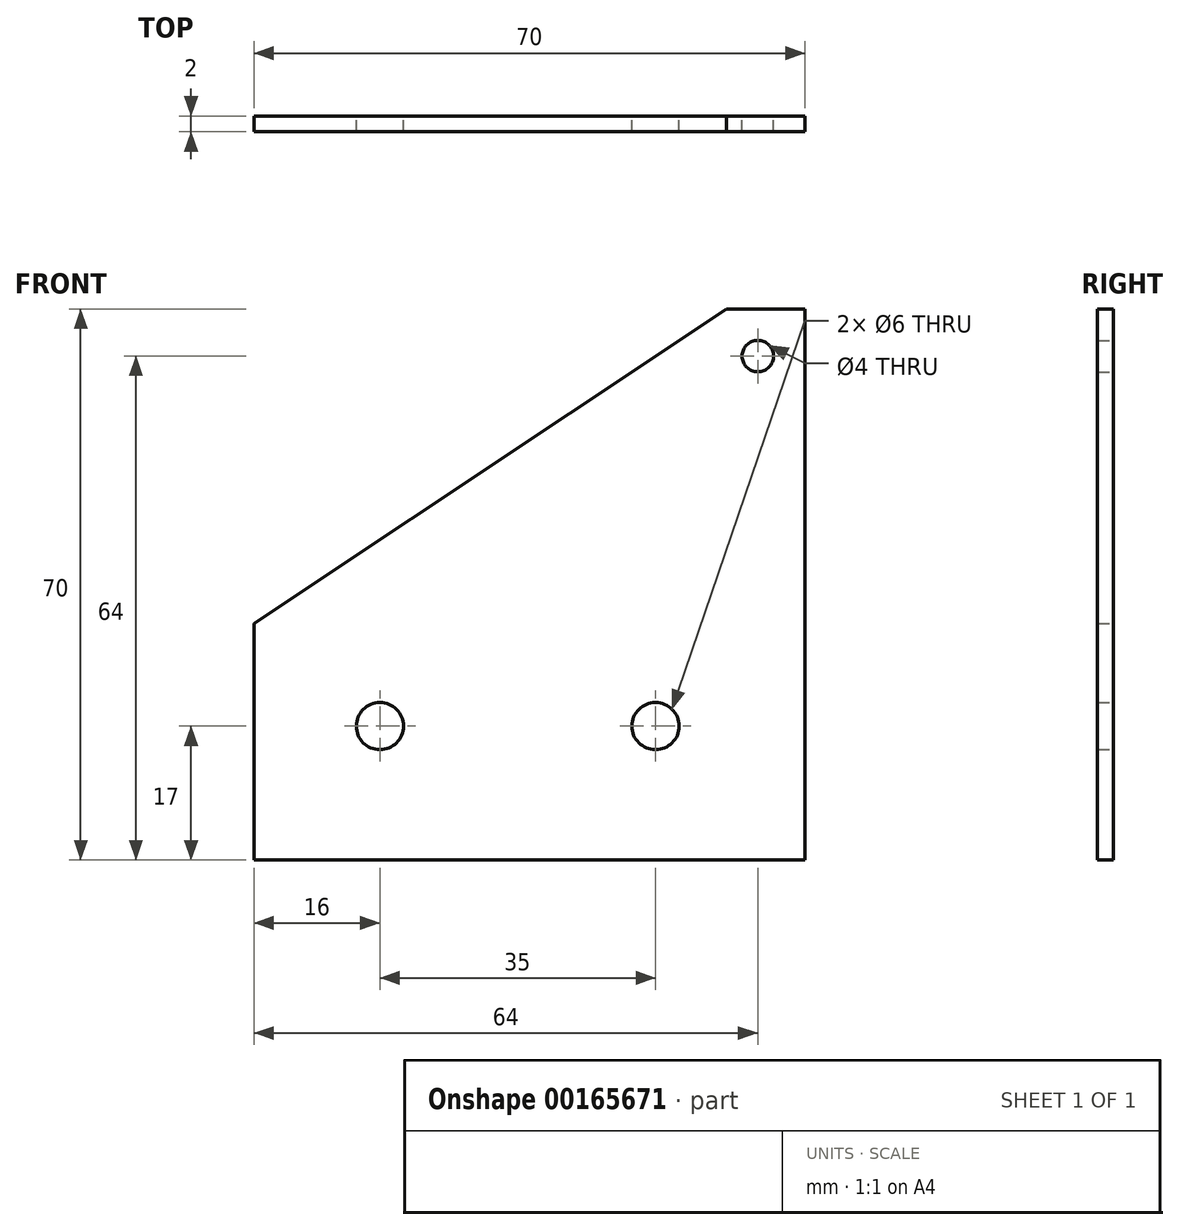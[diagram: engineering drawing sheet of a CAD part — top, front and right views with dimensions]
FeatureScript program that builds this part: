
annotation { "Feature Type Name" : "Feature", "Feature Type Description" : "" }
export const myFeature = defineFeature(function(context is Context, id is Id, definition is map)
    precondition{}
    {
        {
            var Q0;
            Q0=qCreatedBy(makeId("Front.planeOp"),FACE);
            var sketch = newSketch(context, id + "F0", { "sketchPlane" : qUnion([Q0]) });
            skLineSegment(sketch, "E0.bottom", {"start": v(-24.49, 0) * mm, "end": v(45.51, 0) * mm});
            skLineSegment(sketch, "E0.top", {"start": v(-24.49, 0) * mm, "end": v(45.51, 0) * mm});
            skLineSegment(sketch, "E0.left", {"start": v(-24.49, 0) * mm, "end": v(-24.49, 0) * mm});
            skLineSegment(sketch, "E0.right", {"start": v(45.51, 0) * mm, "end": v(45.51, 0) * mm});
            skLineSegment(sketch, "E1", {"start": v(45.51, 0) * mm, "end": v(45.51, 70) * mm});
            skLineSegment(sketch, "E2", {"start": v(45.51, 70) * mm, "end": v(35.51, 70) * mm});
            skLineSegment(sketch, "E3", {"start": v(35.51, 70) * mm, "end": v(-24.49, 30) * mm});
            skLineSegment(sketch, "E4", {"start": v(-24.49, 30) * mm, "end": v(-24.49, 0) * mm});
            skCircle(sketch, "E5", {"center": v(-8.49, 17) * mm, "radius": 3 * mm});
            skCircle(sketch, "E6", {"center": v(26.51, 17) * mm, "radius": 3 * mm});
            skCircle(sketch, "E7", {"center": v(39.51, 64) * mm, "radius": 2 * mm});
            skSolve(sketch);
        }
        {
            var Q0;
            Q0=makeQuery(id+"F0.imprint","IMPRINT",FACE,{"disambiguationData":[TD([[makeQuery(id+"F0.imprint","IMPRINT",EDGE,{"derivedFrom":sQuery(id+"F0.wireOp",EDGE,"E0.bottom")}),1.0]])]});
            extrude(context, id + "F1", {"entities" : qUnion([Q0]), "depth" : 2 * mm, "offsetDistance" : 25 * mm});
        }
    });
